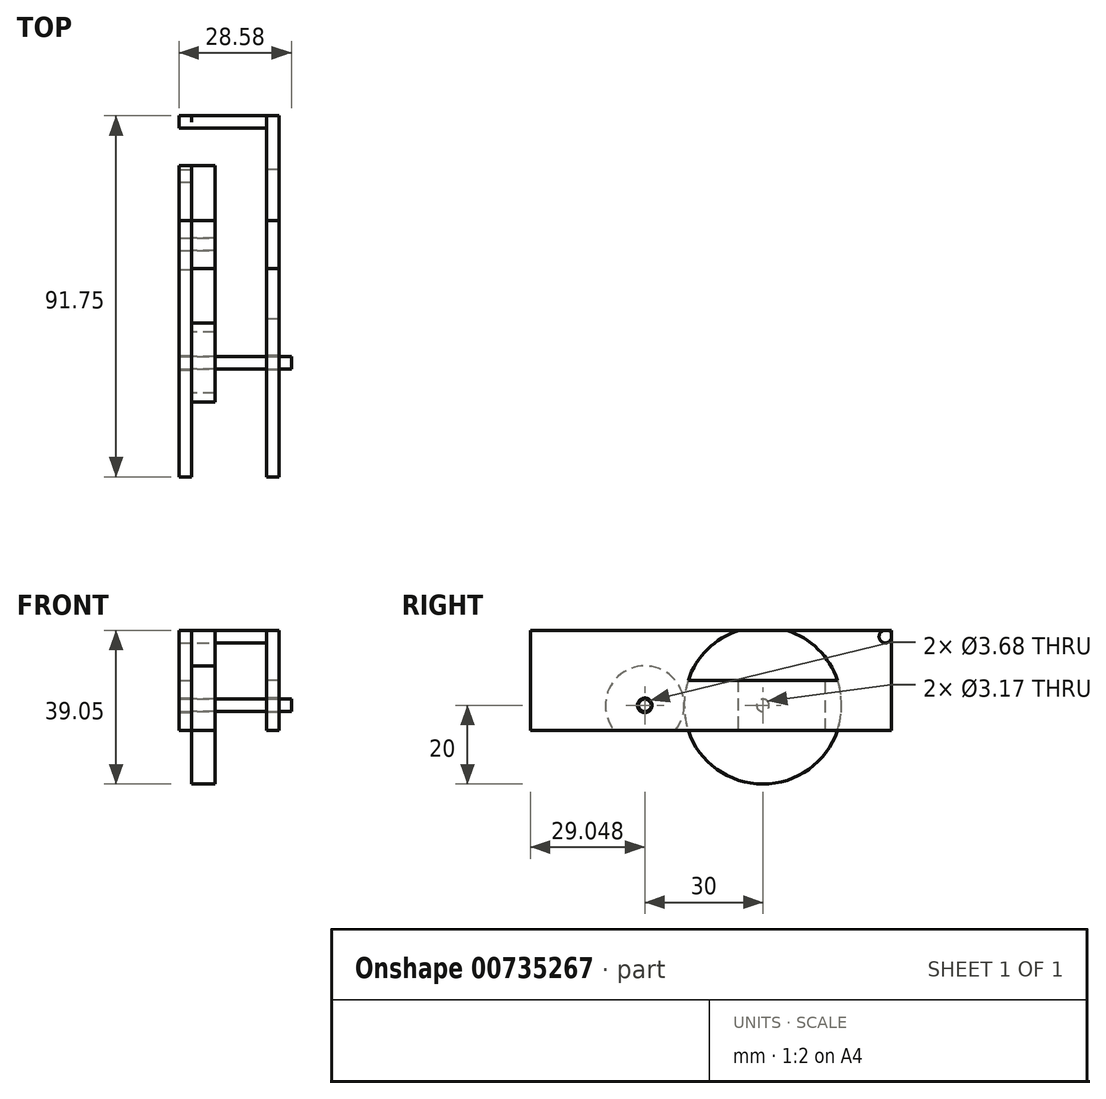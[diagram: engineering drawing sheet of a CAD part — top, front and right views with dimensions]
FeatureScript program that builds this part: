
annotation { "Feature Type Name" : "Feature", "Feature Type Description" : "" }
export const myFeature = defineFeature(function(context is Context, id is Id, definition is map)
    precondition{}
    {
        {
            var Q0;
            Q0=qCreatedBy(makeId("Right.planeOp"),FACE);
            var sketch = newSketch(context, id + "F0", { "sketchPlane" : qUnion([Q0])});
            skLineSegment(sketch, "E0", {"start": v(42.06, 6.35) * mm, "end": v(48.4, 6.35) * mm, "construction": true});
            skCircle(sketch, "E1", {"center": v(48.4, 6.35) * mm, "radius": 20 * mm});
            skLineSegment(sketch, "E2", {"start": v(48.4, 6.35) * mm, "end": v(18.4, 6.35) * mm, "construction": true});
            skCircle(sketch, "E3", {"center": v(18.4, 6.35) * mm, "radius": 10 * mm});
            skCircle(sketch, "E4", {"center": v(18.4, 6.35) * mm, "radius": 1.59 * mm});
            skCircle(sketch, "E5", {"center": v(18.4, 6.35) * mm, "radius": 1.84 * mm});
            skCircle(sketch, "E6", {"center": v(48.4, 6.35) * mm, "radius": 1.59 * mm});
            skCircle(sketch, "E7", {"center": v(48.4, 6.35) * mm, "radius": 1.84 * mm});
            skLineSegment(sketch, "E8.bottom", {"start": v(35.82, 25.4) * mm, "end": v(81.1, 25.4) * mm});
            skLineSegment(sketch, "E8.top", {"start": v(73.49, 0) * mm, "end": v(81.1, 0) * mm});
            skLineSegment(sketch, "E8.right", {"start": v(81.1, 25.4) * mm, "end": v(81.1, 0) * mm});
            skLineSegment(sketch, "E9", {"start": v(8.4, 6.35) * mm, "end": v(-10.64, 6.35) * mm, "construction": true});
            skLineSegment(sketch, "E10", {"start": v(-10.64, 0) * mm, "end": v(-10.64, 25.4) * mm});
            skPoint(sketch, "E11.first.point", {"position": v(79.52, 0) * mm});
            skPoint(sketch, "E11.second.point", {"position": v(81.1, 1.59) * mm});
            skPoint(sketch, "E11.third.point", {"position": v(77.96, 1.9) * mm});
            skCircle(sketch, "E12", {"center": v(79.52, 23.81) * mm, "radius": 1.59 * mm});
            skPoint(sketch, "E12.first.point", {"position": v(79.52, 25.4) * mm});
            skPoint(sketch, "E12.second.point", {"position": v(81.1, 23.81) * mm});
            skPoint(sketch, "E12.third.point", {"position": v(77.97, 23.48) * mm});
            skLineSegment(sketch, "E13.bottom", {"start": v(35.82, 25.4) * mm, "end": v(41.82, 25.4) * mm});
            skLineSegment(sketch, "E13.top", {"start": v(74.28, 0) * mm, "end": v(80.28, 0) * mm});
            skLineSegment(sketch, "E14", {"start": v(-10.64, 25.4) * mm, "end": v(35.82, 25.4) * mm});
            skLineSegment(sketch, "E15", {"start": v(74.28, 0) * mm, "end": v(74.28, 12.7) * mm});
            skLineSegment(sketch, "E16", {"start": v(74.28, 12.7) * mm, "end": v(22.06, 12.7) * mm});
            skPoint(sketch, "E16.endSnap0", {"position": v(22.06, 3.17) * mm});
            skLineSegment(sketch, "E17", {"start": v(22.06, 12.7) * mm, "end": v(22.06, 0) * mm});
            skLineSegment(sketch, "E18", {"start": v(-10.64, 0) * mm, "end": v(81.1, 0) * mm});
            skSolve(sketch);
        }
        {
            var Q0;
            {var subQ7=sQuery(id+"F0.wireOp",EDGE,"E3");Q0=makeQuery(id+"F0.imprint","IMPRINT",FACE,{"disambiguationData":[TD([[makeQuery(id+"F0.imprint","IMPRINT",EDGE,{"derivedFrom":subQ7}),-1.0]])]});}
            var Q1;
            {var subQ0=sQuery(id+"F0.wireOp",EDGE,"E8.right");var subQ1=sQuery(id+"F0.wireOp",EDGE,"E8.bottom");var subQ2=makeQuery(id+"F0.imprint","INTERSECT",VERTEX,{"derivedFrom":[subQ1,subQ0]});Q1=makeQuery(id+"F0.imprint","IMPRINT",FACE,{"disambiguationData":[TD([[makeQuery(id+"F0.imprint","IMPRINT",EDGE,{"disambiguationData":[TD([[subQ2,1.0]])],"derivedFrom":subQ1}),-1.0]])]});}
            var Q2;
            {var subQ0=sQuery(id+"F0.wireOp",EDGE,"E8.right");var subQ1=sQuery(id+"F0.wireOp",EDGE,"E8.top");var subQ2=makeQuery(id+"F0.imprint","INTERSECT",VERTEX,{"derivedFrom":[subQ1,subQ0]});Q2=makeQuery(id+"F0.imprint","IMPRINT",FACE,{"disambiguationData":[TD([[makeQuery(id+"F0.imprint","IMPRINT",EDGE,{"disambiguationData":[TD([[subQ2,1.0]])],"derivedFrom":subQ1}),1.0]])]});}
            var Q3;
            {var subQ0=sQuery(id+"F0.wireOp",EDGE,"E10");var subQ1=sQuery(id+"F0.wireOp",EDGE,"mzH20aDh-REpL-ww0y-ika9-ryDnuCNVRDq3");var subQ2=makeQuery(id+"F0.imprint","INTERSECT",VERTEX,{"derivedFrom":[subQ1,subQ0]});Q3=makeQuery(id+"F0.imprint","IMPRINT",FACE,{"disambiguationData":[TD([[makeQuery(id+"F0.imprint","IMPRINT",EDGE,{"disambiguationData":[TD([[subQ2,1.0]])],"derivedFrom":subQ1}),1.0]])]});}
            var Q4;
            {var subQ0=sQuery(id+"F0.wireOp",EDGE,"E10");var subQ1=sQuery(id+"F0.wireOp",EDGE,"AjtEDcku-NLsd-kfh1-AKqZ-MW7YpeOLVoxd");var subQ2=makeQuery(id+"F0.imprint","INTERSECT",VERTEX,{"derivedFrom":[subQ1,subQ0]});Q4=makeQuery(id+"F0.imprint","IMPRINT",FACE,{"disambiguationData":[TD([[makeQuery(id+"F0.imprint","IMPRINT",EDGE,{"disambiguationData":[TD([[subQ2,-1.0]])],"derivedFrom":subQ1}),1.0]])]});}
            var Q5;
            Q5=makeQuery(id+"F0.imprint","IMPRINT",FACE,{"disambiguationData":[TD([[makeQuery(id+"F0.imprint","IMPRINT",EDGE,{"derivedFrom":sQuery(id+"F0.wireOp",EDGE,"E3")}),1.0]])]});
            var Q6;
            {var subQ0=sQuery(id+"F0.wireOp",EDGE,"E12");var subQ1=sQuery(id+"F0.wireOp",EDGE,"E8.right");var subQ2=makeQuery(id+"F0.imprint","INTERSECT",VERTEX,{"derivedFrom":[subQ1,subQ0]});Q6=makeQuery(id+"F0.imprint","IMPRINT",FACE,{"disambiguationData":[TD([[makeQuery(id+"F0.imprint","IMPRINT",EDGE,{"disambiguationData":[TD([[subQ2,-1.0]])],"derivedFrom":subQ1}),-1.0]])]});}
            var Q7;
            {var subQ0=sQuery(id+"F0.wireOp",EDGE,"E13.top");var subQ1=sQuery(id+"F0.wireOp",EDGE,"E11");var subQ2=makeQuery(id+"F0.imprint","INTERSECT",VERTEX,{"derivedFrom":[subQ1,subQ0]});Q7=makeQuery(id+"F0.imprint","IMPRINT",FACE,{"disambiguationData":[TD([[makeQuery(id+"F0.imprint","IMPRINT",EDGE,{"disambiguationData":[TD([[subQ2,1.0]])],"derivedFrom":subQ1}),-1.0]])]});}
            var Q8;
            {var subQ0=sQuery(id+"F0.wireOp",EDGE,"E13.top");var subQ1=sQuery(id+"F0.wireOp",EDGE,"E8.right");var subQ2=makeQuery(id+"F0.imprint","INTERSECT",VERTEX,{"derivedFrom":[subQ1,subQ0]});Q8=makeQuery(id+"F0.imprint","IMPRINT",FACE,{"disambiguationData":[TD([[makeQuery(id+"F0.imprint","IMPRINT",EDGE,{"disambiguationData":[TD([[subQ2,1.0]])],"derivedFrom":subQ1}),-1.0]])]});}
            var Q9;
            {var subQ0=sQuery(id+"F0.wireOp",EDGE,"E13.bottom");var subQ1=sQuery(id+"F0.wireOp",EDGE,"E12");var subQ2=makeQuery(id+"F0.imprint","INTERSECT",VERTEX,{"derivedFrom":[subQ1,subQ0]});Q9=makeQuery(id+"F0.imprint","IMPRINT",FACE,{"disambiguationData":[TD([[makeQuery(id+"F0.imprint","IMPRINT",EDGE,{"disambiguationData":[TD([[subQ2,-1.0]])],"derivedFrom":subQ1}),-1.0]])]});}
            var Q10;
            {var subQ0=sQuery(id+"F0.wireOp",EDGE,"E13.bottom");var subQ1=sQuery(id+"F0.wireOp",EDGE,"E8.right");var subQ2=makeQuery(id+"F0.imprint","INTERSECT",VERTEX,{"derivedFrom":[subQ1,subQ0]});Q10=makeQuery(id+"F0.imprint","IMPRINT",FACE,{"disambiguationData":[TD([[makeQuery(id+"F0.imprint","IMPRINT",EDGE,{"disambiguationData":[TD([[subQ2,-1.0]])],"derivedFrom":subQ1}),-1.0]])]});}
            var Q11;
            {var subQ0=sQuery(id+"F0.wireOp",EDGE,"E14");var subQ1=sQuery(id+"F0.wireOp",EDGE,"E10");var subQ2=makeQuery(id+"F0.imprint","INTERSECT",VERTEX,{"derivedFrom":[subQ1,subQ0]});Q11=makeQuery(id+"F0.imprint","IMPRINT",FACE,{"disambiguationData":[TD([[makeQuery(id+"F0.imprint","IMPRINT",EDGE,{"disambiguationData":[TD([[subQ2,1.0]])],"derivedFrom":subQ1}),-1.0]])]});}
            var Q12;
            {var subQ0=sQuery(id+"F0.wireOp",EDGE,"E17");Q12=makeQuery(id+"F0.imprint","IMPRINT",FACE,{"disambiguationData":[TD([[makeQuery(id+"F0.imprint","IMPRINT",EDGE,{"derivedFrom":subQ0}),-1.0]])]});}
            var Q13;
            {var subQ0=sQuery(id+"F0.wireOp",EDGE,"E15");Q13=makeQuery(id+"F0.imprint","IMPRINT",FACE,{"disambiguationData":[TD([[makeQuery(id+"F0.imprint","IMPRINT",EDGE,{"derivedFrom":subQ0}),1.0]])]});}
            var Q14;
            Q14=makeQuery(id+"F0.imprint","IMPRINT",FACE,{"disambiguationData":[TD([[makeQuery(id+"F0.imprint","IMPRINT",EDGE,{"derivedFrom":sQuery(id+"F0.wireOp",EDGE,"E7")}),-1.0]])]});
            var Q15;
            Q15=makeQuery(id+"F0.imprint","IMPRINT",FACE,{"disambiguationData":[TD([[makeQuery(id+"F0.imprint","IMPRINT",EDGE,{"derivedFrom":sQuery(id+"F0.wireOp",EDGE,"E6")}),1.0]])]});
            var Q16;
            Q16=makeQuery(id+"F0.imprint","IMPRINT",FACE,{"disambiguationData":[TD([[makeQuery(id+"F0.imprint","IMPRINT",EDGE,{"derivedFrom":sQuery(id+"F0.wireOp",EDGE,"E6")}),-1.0]])]});
            var Q17;
            {var subQ0=sQuery(id+"F0.wireOp",EDGE,"E11");var subQ1=makeQuery(id+"F0.imprint","INTERSECT",VERTEX,{"derivedFrom":[sQuery(id+"F0.wireOp",EDGE,"E8.right"),subQ0]});Q17=makeQuery(id+"F0.imprint","IMPRINT",FACE,{"disambiguationData":[TD([[makeQuery(id+"F0.imprint","IMPRINT",EDGE,{"disambiguationData":[TD([[subQ1,-1.0]])],"derivedFrom":subQ0}),1.0]])]});}
            var Q18;
            {var subQ0=sQuery(id+"F0.wireOp",EDGE,"E12");var subQ1=makeQuery(id+"F0.imprint","INTERSECT",VERTEX,{"derivedFrom":[sQuery(id+"F0.wireOp",EDGE,"E8.bottom"),subQ0]});Q18=makeQuery(id+"F0.imprint","IMPRINT",FACE,{"disambiguationData":[TD([[makeQuery(id+"F0.imprint","IMPRINT",EDGE,{"disambiguationData":[TD([[subQ1,1.0]])],"derivedFrom":subQ0}),1.0]])]});}
            var Q19;
            {var subQ0=sQuery(id+"F0.wireOp",EDGE,"1ad34039-b210-4e6b-b085-ae97cf70f0cc");var subQ1=makeQuery(id+"F0.imprint","INTERSECT",VERTEX,{"derivedFrom":[sQuery(id+"F0.wireOp",EDGE,"E10"),subQ0]});Q19=makeQuery(id+"F0.imprint","IMPRINT",FACE,{"disambiguationData":[TD([[makeQuery(id+"F0.imprint","IMPRINT",EDGE,{"disambiguationData":[TD([[subQ1,1.0]])],"derivedFrom":subQ0}),1.0]])]});}
            var Q20;
            {var subQ0=sQuery(id+"F0.wireOp",EDGE,"6cbd52c8-ad08-4bfb-b3ed-cb9e27654880");var subQ1=makeQuery(id+"F0.imprint","INTERSECT",VERTEX,{"derivedFrom":[sQuery(id+"F0.wireOp",EDGE,"E10"),subQ0]});Q20=makeQuery(id+"F0.imprint","IMPRINT",FACE,{"disambiguationData":[TD([[makeQuery(id+"F0.imprint","IMPRINT",EDGE,{"disambiguationData":[TD([[subQ1,-1.0]])],"derivedFrom":subQ0}),1.0]])]});}
            extrude(context, id + "F1", {"entities" : qUnion([Q0, Q1, Q2, Q3, Q4, Q5, Q6, Q7, Q8, Q9, Q10, Q11, Q12, Q13, Q14, Q15, Q16, Q17, Q18, Q19, Q20]), "depth" : 3.17 * mm, "offsetDistance" : 25.4 * mm});
        }
        {
            var Q0;
            {var subQ0=sQuery(id+"F0.wireOp",EDGE,"E12");var subQ1=makeQuery(id+"F0.imprint","INTERSECT",VERTEX,{"derivedFrom":[sQuery(id+"F0.wireOp",EDGE,"E8.bottom"),subQ0]});Q0=makeQuery(id+"F0.imprint","IMPRINT",FACE,{"disambiguationData":[TD([[makeQuery(id+"F0.imprint","IMPRINT",EDGE,{"disambiguationData":[TD([[subQ1,1.0]])],"derivedFrom":subQ0}),1.0]])]});}
            var Q1;
            {var subQ0=sQuery(id+"F0.wireOp",EDGE,"E11");var subQ1=makeQuery(id+"F0.imprint","INTERSECT",VERTEX,{"derivedFrom":[sQuery(id+"F0.wireOp",EDGE,"E8.top"),subQ0]});Q1=makeQuery(id+"F0.imprint","IMPRINT",FACE,{"disambiguationData":[TD([[makeQuery(id+"F0.imprint","IMPRINT",EDGE,{"disambiguationData":[TD([[subQ1,1.0]])],"derivedFrom":subQ0}),1.0]])]});}
            var Q2;
            {var subQ0=sQuery(id+"F0.wireOp",EDGE,"6cbd52c8-ad08-4bfb-b3ed-cb9e27654880");var subQ1=makeQuery(id+"F0.imprint","INTERSECT",VERTEX,{"derivedFrom":[sQuery(id+"F0.wireOp",EDGE,"AjtEDcku-NLsd-kfh1-AKqZ-MW7YpeOLVoxd"),subQ0]});Q2=makeQuery(id+"F0.imprint","IMPRINT",FACE,{"disambiguationData":[TD([[makeQuery(id+"F0.imprint","IMPRINT",EDGE,{"disambiguationData":[TD([[subQ1,1.0]])],"derivedFrom":subQ0}),1.0]])]});}
            var Q3;
            {var subQ0=sQuery(id+"F0.wireOp",EDGE,"1ad34039-b210-4e6b-b085-ae97cf70f0cc");var subQ1=makeQuery(id+"F0.imprint","INTERSECT",VERTEX,{"derivedFrom":[sQuery(id+"F0.wireOp",EDGE,"mzH20aDh-REpL-ww0y-ika9-ryDnuCNVRDq3"),subQ0]});Q3=makeQuery(id+"F0.imprint","IMPRINT",FACE,{"disambiguationData":[TD([[makeQuery(id+"F0.imprint","IMPRINT",EDGE,{"disambiguationData":[TD([[subQ1,-1.0]])],"derivedFrom":subQ0}),1.0]])]});}
            extrude(context, id + "F2", {"entities" : qUnion([Q0, Q1, Q2, Q3]), "oppositeDirection" : true, "depth" : 19.05 * mm, "offsetDistance" : 25.4 * mm});
        }
        {
            var Q0;
            Q0=makeQuery(id+"F2.opExtrude","CAP_FACE",FACE,{"disambiguationData":[OSD([sQuery(id+"F0.wireOp",EDGE,"E12")])],"isStart":false});
            var sketch = newSketch(context, id + "F3", { "sketchPlane" : qUnion([Q0])});
            skLineSegment(sketch, "E19.bottom", {"start": v(-81.1, 25.4) * mm, "end": v(10.64, 25.4) * mm});
            skLineSegment(sketch, "E19.top", {"start": v(-81.1, 0) * mm, "end": v(10.64, 0) * mm});
            skLineSegment(sketch, "E19.left", {"start": v(-81.1, 25.4) * mm, "end": v(-81.1, 0) * mm});
            skLineSegment(sketch, "E19.right", {"start": v(10.64, 25.4) * mm, "end": v(10.64, 0) * mm});
            skLineSegment(sketch, "E20", {"start": v(-64.28, 6.35) * mm, "end": v(-64.28, 0) * mm, "construction": true});
            skLineSegment(sketch, "E21", {"start": v(-64.28, 6.35) * mm, "end": v(-42.06, 6.35) * mm, "construction": true});
            skLineSegment(sketch, "E22", {"start": v(-42.06, 6.35) * mm, "end": v(-42.06, 0) * mm, "construction": true});
            skLineSegment(sketch, "E23", {"start": v(-42.06, 6.35) * mm, "end": v(-48.4, 6.35) * mm});
            skCircle(sketch, "E24", {"center": v(-48.4, 6.35) * mm, "radius": 20 * mm});
            skLineSegment(sketch, "E25", {"start": v(-48.4, 6.35) * mm, "end": v(-18.4, 6.35) * mm, "construction": true});
            skCircle(sketch, "E26", {"center": v(-18.4, 6.35) * mm, "radius": 10 * mm});
            skCircle(sketch, "E27", {"center": v(-18.4, 6.35) * mm, "radius": 1.59 * mm});
            skCircle(sketch, "E28", {"center": v(-18.4, 6.35) * mm, "radius": 1.84 * mm});
            skCircle(sketch, "E29", {"center": v(-48.4, 6.35) * mm, "radius": 1.84 * mm});
            skCircle(sketch, "E30", {"center": v(-48.4, 6.35) * mm, "radius": 1.59 * mm});
            skLineSegment(sketch, "E31", {"start": v(-64.28, 0) * mm, "end": v(-64.28, 12.7) * mm});
            skLineSegment(sketch, "E32", {"start": v(-64.28, 12.7) * mm, "end": v(-42.06, 12.7) * mm});
            skLineSegment(sketch, "E33", {"start": v(-42.06, 12.7) * mm, "end": v(-42.06, 0) * mm});
            skSolve(sketch);
        }
        {
            var Q0;
            {var subQ0=sQuery(id+"F3.wireOp",EDGE,"61rDZBB9-DkLB-R1jF-Ugw1-9J4s0qTPQNlm");var subQ1=sQuery(id+"F3.wireOp",EDGE,"E19.top");var subQ2=makeQuery(id+"F3.imprint","INTERSECT",VERTEX,{"disambiguationData":[OD(0.0)],"derivedFrom":[subQ1,subQ0]});Q0=makeQuery(id+"F3.imprint","IMPRINT",FACE,{"disambiguationData":[TD([[makeQuery(id+"F3.imprint","IMPRINT",EDGE,{"disambiguationData":[TD([[subQ2,-1.0]])],"derivedFrom":subQ1}),1.0]])]});}
            var Q1;
            Q1=makeQuery(id+"F3.imprint","IMPRINT",FACE,{"disambiguationData":[TD([[makeQuery(id+"F3.imprint","IMPRINT",EDGE,{"derivedFrom":sQuery(id+"F3.wireOp",EDGE,"f6RzX2im-ddRW-lgic-JvNA-CsLhbOmZ7d9f")}),1.0]])]});
            var Q2;
            {var subQ0=sQuery(id+"F3.wireOp",EDGE,"E19.right");Q2=makeQuery(id+"F3.imprint","IMPRINT",FACE,{"disambiguationData":[TD([[makeQuery(id+"F3.imprint","IMPRINT",EDGE,{"derivedFrom":subQ0}),-1.0]])]});}
            var Q3;
            {var subQ0=sQuery(id+"F3.wireOp",EDGE,"E19.left");var subQ1=sQuery(id+"F3.wireOp",EDGE,"E19.bottom");var subQ2=makeQuery(id+"F3.imprint","INTERSECT",VERTEX,{"derivedFrom":[subQ1,subQ0]});Q3=makeQuery(id+"F3.imprint","IMPRINT",FACE,{"disambiguationData":[TD([[makeQuery(id+"F3.imprint","IMPRINT",EDGE,{"disambiguationData":[TD([[subQ2,-1.0]])],"derivedFrom":subQ1}),-1.0]])]});}
            var Q4;
            {var subQ0=makeQuery(id+"F2.opExtrude","CAP_EDGE",EDGE,{"disambiguationData":[OSD([sQuery(id+"F0.wireOp",EDGE,"E12")])],"isStart":false});var subQ1=makeQuery(id+"F3.imprint","INTERSECT",VERTEX,{"derivedFrom":[subQ0,sQuery(id+"F3.wireOp",EDGE,"E19.bottom")]});Q4=makeQuery(id+"F3.imprint","IMPRINT",FACE,{"disambiguationData":[TD([[makeQuery(id+"F3.imprint","IMPRINT",EDGE,{"disambiguationData":[TD([[subQ1,1.0]])],"derivedFrom":subQ0}),-1.0]])]});}
            var Q5;
            Q5=makeQuery(id+"F3.imprint","IMPRINT",FACE,{"disambiguationData":[TD([[makeQuery(id+"F3.imprint","IMPRINT",EDGE,{"derivedFrom":sQuery(id+"F3.wireOp",EDGE,"E26")}),1.0]])]});
            var Q6;
            {var subQ0=sQuery(id+"F3.wireOp",EDGE,"E33");var subQ9=makeQuery(id+"F3.imprint","IMPRINT",VERTEX,{"derivedFrom":subQ0});Q6=makeQuery(id+"F3.imprint","IMPRINT",FACE,{"disambiguationData":[TD([[makeQuery(id+"F3.imprint","IMPRINT",EDGE,{"disambiguationData":[TD([[subQ9,1.0]])],"derivedFrom":subQ0}),1.0]])]});}
            var Q7;
            {var subQ5=sQuery(id+"F3.wireOp",EDGE,"E24");var subQ6=sQuery(id+"F3.wireOp",EDGE,"E19.bottom");var subQ7=makeQuery(id+"F3.imprint","INTERSECT",VERTEX,{"disambiguationData":[OD(0.0)],"derivedFrom":[subQ6,subQ5]});Q7=makeQuery(id+"F3.imprint","IMPRINT",FACE,{"disambiguationData":[TD([[makeQuery(id+"F3.imprint","IMPRINT",EDGE,{"disambiguationData":[TD([[subQ7,1.0]])],"derivedFrom":subQ6}),-1.0]])]});}
            var Q8;
            {var subQ0=sQuery(id+"F3.wireOp",EDGE,"E24");var subQ1=sQuery(id+"F3.wireOp",EDGE,"E19.top");var subQ2=makeQuery(id+"F3.imprint","INTERSECT",VERTEX,{"disambiguationData":[OD(1.0)],"derivedFrom":[subQ1,subQ0]});Q8=makeQuery(id+"F3.imprint","IMPRINT",FACE,{"disambiguationData":[TD([[makeQuery(id+"F3.imprint","IMPRINT",EDGE,{"disambiguationData":[TD([[subQ2,-1.0]])],"derivedFrom":subQ1}),1.0]])]});}
            extrude(context, id + "F4", {"entities" : qUnion([Q0, Q1, Q2, Q3, Q4, Q5, Q6, Q7, Q8]), "operationType" : NewBodyOperationType.ADD, "depth" : 3.17 * mm, "offsetDistance" : 25.4 * mm});
        }
        {
            var Q0;
            Q0=makeQuery(id+"F3.imprint","IMPRINT",FACE,{"disambiguationData":[TD([[makeQuery(id+"F3.imprint","IMPRINT",EDGE,{"derivedFrom":sQuery(id+"F3.wireOp",EDGE,"E30")}),1.0]])]});
            extrude(context, id + "F5", {"entities" : qUnion([Q0]), "depth" : 3.17 * mm, "offsetDistance" : 25.4 * mm});
        }
        {
            var Q0;
            Q0=makeQuery(id+"F3.imprint","IMPRINT",FACE,{"disambiguationData":[TD([[makeQuery(id+"F3.imprint","IMPRINT",EDGE,{"derivedFrom":sQuery(id+"F3.wireOp",EDGE,"E30")}),1.0]])]});
            extrude(context, id + "F6", {"entities" : qUnion([Q0]), "operationType" : NewBodyOperationType.ADD, "oppositeDirection" : true, "depth" : 6 * mm, "offsetDistance" : 25.4 * mm});
        }
        {
            var Q0;
            {var subQ0=sQuery(id+"F3.wireOp",EDGE,"E24");var subQ1=sQuery(id+"F3.wireOp",EDGE,"E19.top");var subQ2=makeQuery(id+"F3.imprint","INTERSECT",VERTEX,{"disambiguationData":[OD(0.0)],"derivedFrom":[subQ1,subQ0]});Q0=makeQuery(id+"F3.imprint","IMPRINT",FACE,{"disambiguationData":[TD([[makeQuery(id+"F3.imprint","IMPRINT",EDGE,{"disambiguationData":[TD([[subQ2,-1.0]])],"derivedFrom":subQ1}),-1.0]])]});}
            var Q1;
            Q1=makeQuery(id+"F3.imprint","IMPRINT",FACE,{"disambiguationData":[TD([[makeQuery(id+"F3.imprint","IMPRINT",EDGE,{"derivedFrom":sQuery(id+"F3.wireOp",EDGE,"E29")}),-1.0]])]});
            var Q2;
            Q2=makeQuery(id+"F3.imprint","IMPRINT",FACE,{"disambiguationData":[TD([[makeQuery(id+"F3.imprint","IMPRINT",EDGE,{"derivedFrom":sQuery(id+"F3.wireOp",EDGE,"E29")}),1.0]])]});
            var Q3;
            {var subQ0=sQuery(id+"F3.wireOp",EDGE,"E33");var subQ9=makeQuery(id+"F3.imprint","IMPRINT",VERTEX,{"derivedFrom":subQ0});Q3=makeQuery(id+"F3.imprint","IMPRINT",FACE,{"disambiguationData":[TD([[makeQuery(id+"F3.imprint","IMPRINT",EDGE,{"disambiguationData":[TD([[subQ9,1.0]])],"derivedFrom":subQ0}),1.0]])]});}
            var Q4;
            {var subQ0=sQuery(id+"F3.wireOp",EDGE,"E24");var subQ1=sQuery(id+"F3.wireOp",EDGE,"E19.bottom");var subQ2=makeQuery(id+"F3.imprint","INTERSECT",VERTEX,{"disambiguationData":[OD(0.0)],"derivedFrom":[subQ1,subQ0]});Q4=makeQuery(id+"F3.imprint","IMPRINT",FACE,{"disambiguationData":[TD([[makeQuery(id+"F3.imprint","IMPRINT",EDGE,{"disambiguationData":[TD([[subQ2,-1.0]])],"derivedFrom":subQ1}),1.0]])]});}
            extrude(context, id + "F7", {"entities" : qUnion([Q0, Q1, Q2, Q3, Q4]), "oppositeDirection" : true, "depth" : 6 * mm, "offsetDistance" : 25.4 * mm});
        }
        {
            var Q0;
            Q0=makeQuery(id+"F3.imprint","IMPRINT",FACE,{"disambiguationData":[TD([[makeQuery(id+"F3.imprint","IMPRINT",EDGE,{"derivedFrom":sQuery(id+"F3.wireOp",EDGE,"E27")}),1.0]])]});
            extrude(context, id + "F8", {"entities" : qUnion([Q0]), "depth" : 3.17 * mm, "offsetDistance" : 25.4 * mm});
        }
        {
            var Q0;
            Q0=makeQuery(id+"F3.imprint","IMPRINT",FACE,{"disambiguationData":[TD([[makeQuery(id+"F3.imprint","IMPRINT",EDGE,{"derivedFrom":sQuery(id+"F3.wireOp",EDGE,"E27")}),1.0]])]});
            extrude(context, id + "F9", {"entities" : qUnion([Q0]), "operationType" : NewBodyOperationType.ADD, "oppositeDirection" : true, "depth" : 25.4 * mm, "offsetDistance" : 25.4 * mm});
        }
        {
            var Q0;
            Q0=makeQuery(id+"F3.imprint","IMPRINT",FACE,{"disambiguationData":[TD([[makeQuery(id+"F3.imprint","IMPRINT",EDGE,{"derivedFrom":sQuery(id+"F3.wireOp",EDGE,"E26")}),1.0]])]});
            var Q1;
            Q1=makeQuery(id+"F3.imprint","IMPRINT",FACE,{"disambiguationData":[TD([[makeQuery(id+"F3.imprint","IMPRINT",EDGE,{"derivedFrom":sQuery(id+"F3.wireOp",EDGE,"E27")}),-1.0]])]});
            var Q2;
            {var subQ0=sQuery(id+"F3.wireOp",EDGE,"E26");var subQ1=sQuery(id+"F3.wireOp",EDGE,"E19.top");var subQ2=makeQuery(id+"F3.imprint","INTERSECT",VERTEX,{"disambiguationData":[OD(0.0)],"derivedFrom":[subQ1,subQ0]});Q2=makeQuery(id+"F3.imprint","IMPRINT",FACE,{"disambiguationData":[TD([[makeQuery(id+"F3.imprint","IMPRINT",EDGE,{"disambiguationData":[TD([[subQ2,-1.0]])],"derivedFrom":subQ1}),-1.0]])]});}
            extrude(context, id + "F10", {"entities" : qUnion([Q0, Q1, Q2]), "oppositeDirection" : true, "depth" : 6 * mm, "offsetDistance" : 25.4 * mm});
        }
    });
